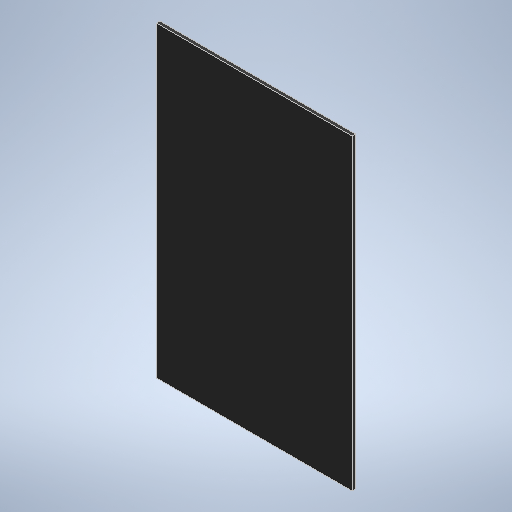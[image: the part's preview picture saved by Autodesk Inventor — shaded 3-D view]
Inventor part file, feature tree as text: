
AUTODESK INVENTOR PART (.ipt)
format: ipt  version: 2025 (Build 290162010, 162A)  size: 213,504 bytes
history: native  units: in
note: dims shown in document units (in); Inventor stores cm internally (conversion verified against a paired STEP export)
features: extrude x1, sketch x1
ambient origin geometry x8: Origin, YZ Plane, XZ Plane, XY Plane, X Axis, Y Axis, Z Axis, Center Point
bodies: Solid1 (feature_tree)
feature tree (2):
  extrude  "Extrusion1"  Depth=3.5in
  sketch  "Sketch1"  dims[d1=5.5in d2=3.5in d3=0.0625in d4=0.0in]
